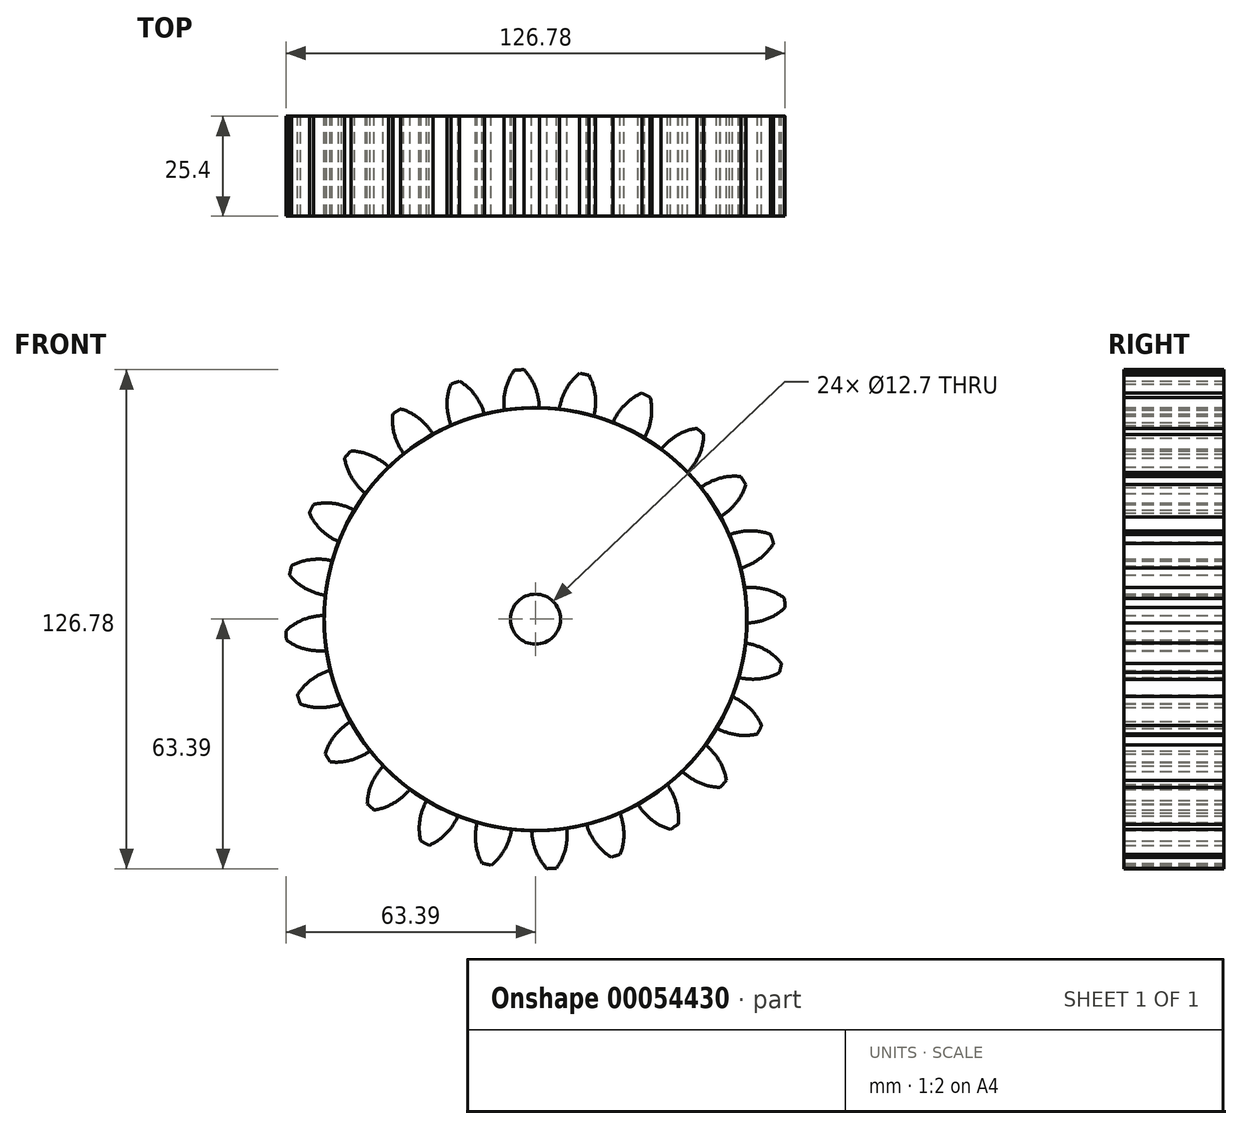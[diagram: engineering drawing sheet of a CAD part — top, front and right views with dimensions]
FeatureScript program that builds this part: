
annotation { "Feature Type Name" : "Feature", "Feature Type Description" : "" }
export const myFeature = defineFeature(function(context is Context, id is Id, definition is map)
    precondition{}
    {
        {
            var Q0;
            Q0=qCreatedBy(makeId("Front.planeOp"),FACE);
            var sketch = newSketch(context, id + "F0", { "sketchPlane" : qUnion([Q0])});
            skCircle(sketch, "E0", {"center": v(0, 0) * mm, "radius": 63.5 * mm, "construction": true});
            skCircle(sketch, "E1", {"center": v(0, 0) * mm, "radius": 58.67 * mm, "construction": true});
            skCircle(sketch, "E2", {"center": v(0, 0) * mm, "radius": 53.72 * mm});
            skLineSegment(sketch, "E3", {"start": v(0, 0) * mm, "end": v(0, 175.81) * mm, "construction": true});
            skLineSegment(sketch, "E4", {"start": v(0, 0) * mm, "end": v(-11.52, 175.81) * mm, "construction": true});
            skLineSegment(sketch, "E5", {"start": v(0, 58.67) * mm, "end": v(-79.4, 58.67) * mm, "construction": true});
            skLineSegment(sketch, "E6", {"start": v(0, 58.67) * mm, "end": v(-79.4, 29.77) * mm, "construction": true});
            skCircle(sketch, "E7", {"center": v(0, 0) * mm, "radius": 55.14 * mm, "construction": true});
            skCircle(sketch, "E8", {"center": v(0, 58.67) * mm, "radius": 14.6 * mm, "construction": true});
            skCircle(sketch, "E9", {"center": v(-13.63, 53.42) * mm, "radius": 14.6 * mm, "construction": true});
            skArc(sketch, "E10", {"start": v(0, 58.67) * mm, "mid": v(-1.24, 61.2) * mm, "end": v(-2.99, 63.43) * mm});
            skArc(sketch, "E11", {"start": v(0.97, 53.71) * mm, "mid": v(0.68, 56.23) * mm, "end": v(0, 58.67) * mm});
            skArc(sketch, "E12.MirrorCS", {"start": v(-7.66, 58.17) * mm, "mid": v(-6.76, 60.85) * mm, "end": v(-5.32, 63.28) * mm});
            skArc(sketch, "E13.MirrorCS", {"start": v(-7.98, 53.13) * mm, "mid": v(-8.02, 55.66) * mm, "end": v(-7.66, 58.17) * mm});
            skArc(sketch, "E14", {"start": v(-2.95, 63.4) * mm, "mid": v(-4.13, 63.34) * mm, "end": v(-5.32, 63.28) * mm});
            skCircle(sketch, "E15", {"center": v(0, 0) * mm, "radius": 6.35 * mm});
            skSolve(sketch);
        }
        {
            var Q0;
            {var subQ0=sQuery(id+"F0.wireOp",EDGE,"E2");var subQ1=makeQuery(id+"F0.imprint","INTERSECT",VERTEX,{"derivedFrom":[subQ0,sQuery(id+"F0.wireOp",EDGE,"E11")]});Q0=makeQuery(id+"F0.imprint","IMPRINT",FACE,{"disambiguationData":[TD([[makeQuery(id+"F0.imprint","IMPRINT",EDGE,{"disambiguationData":[TD([[subQ1,-1.0]])],"derivedFrom":subQ0}),1.0]])]});}
            var Q1;
            {var subQ0=sQuery(id+"F0.wireOp",EDGE,"E11");Q1=makeQuery(id+"F0.imprint","IMPRINT",FACE,{"disambiguationData":[TD([[makeQuery(id+"F0.imprint","IMPRINT",EDGE,{"derivedFrom":subQ0}),1.0]])]});}
            extrude(context, id + "F1", {"entities" : qUnion([Q0, Q1]), "depth" : 25.4 * mm});
        }
        {
            var Q0;
            Q0=makeQuery(id+"F1.opExtrude","SWEPT_BODY",BODY,{"disambiguationData":[OSD([sQuery(id+"F0.wireOp",EDGE,"E2"),sQuery(id+"F0.wireOp",EDGE,"E10"),sQuery(id+"F0.wireOp",EDGE,"E11"),sQuery(id+"F0.wireOp",EDGE,"E12.MirrorCS"),sQuery(id+"F0.wireOp",EDGE,"E13.MirrorCS"),sQuery(id+"F0.wireOp",EDGE,"E14")])]});
            var Q1;
            Q1=makeQuery(id+"F1.opExtrude","SWEPT_FACE",FACE,{"disambiguationData":[OSD([sQuery(id+"F0.wireOp",EDGE,"E2")])]});
            circularPattern(context, id + "F2", {"entities" : qUnion([Q0]), "axis" : qUnion([Q1]), "angle" : 15 * degree, "instanceCount" : 24});
        }
    });
